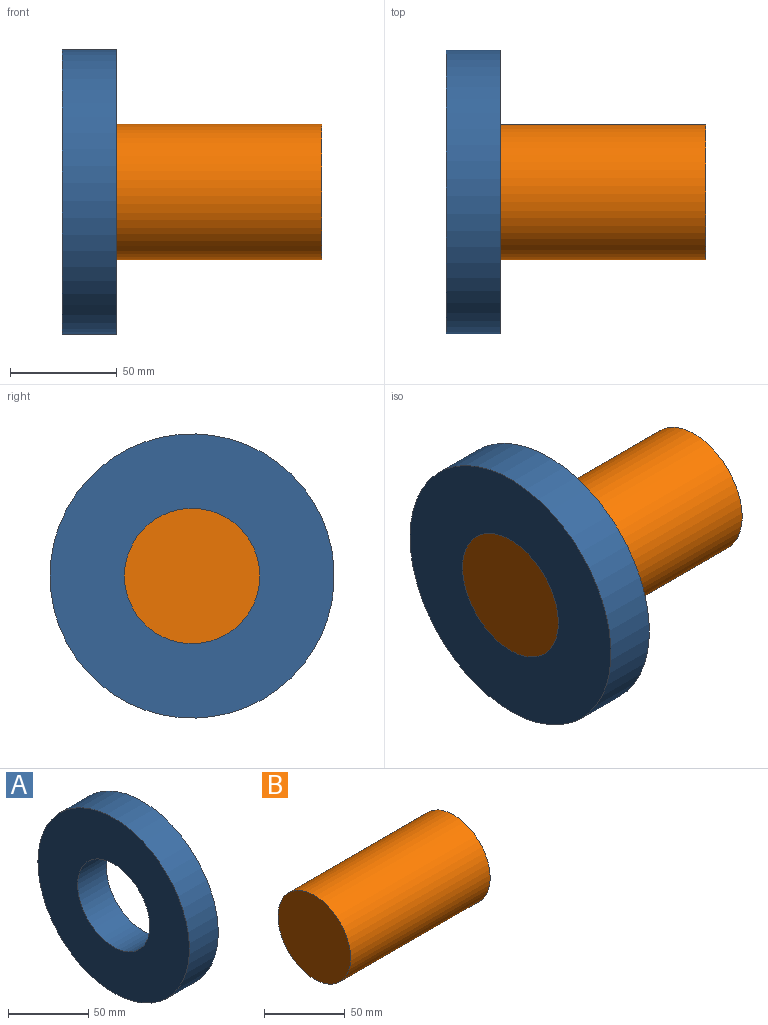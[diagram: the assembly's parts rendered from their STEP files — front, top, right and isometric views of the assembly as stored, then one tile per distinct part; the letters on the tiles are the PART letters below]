
ASSEMBLY  parts=2 mates=1
PART A: 4 faces, bbox 25.4x133.4x133.4 mm
  f0: cylinder r=31.75mm len=63.5mm, axis (1,0,0), area 5067.1mm2, adj f2,f3
  f1: cylinder r=66.67mm len=133.35mm, axis (1,0,0), area 10640.9mm2, adj f2,f3
  f2: plane 133.35x133.35mm, normal (-1,0,0), area 10799.2mm2, adj f0,f1
  f3: plane 133.35x133.35mm, normal (1,0,0), area 10799.2mm2, adj f0,f1
PART B: 3 faces, bbox 121.9x63.5x63.5 mm
  f0: cylinder r=31.75mm len=121.92mm, axis (-1,0,0), area 24322mm2, adj f1,f2
  f1: plane 63.5x63.5mm, normal (1,0,0), area 3166.9mm2, adj f0
  f2: plane 63.5x63.5mm, normal (-1,0,0), area 3166.9mm2, adj f0
PLACE A t=(-2242.82,0,0)mm fixed
PLACE B t=(-2268.22,0,0)mm
MATE fastened A.f0 <-> B.f0  axis (-1,0,0) through (17.78,0,0)mm
